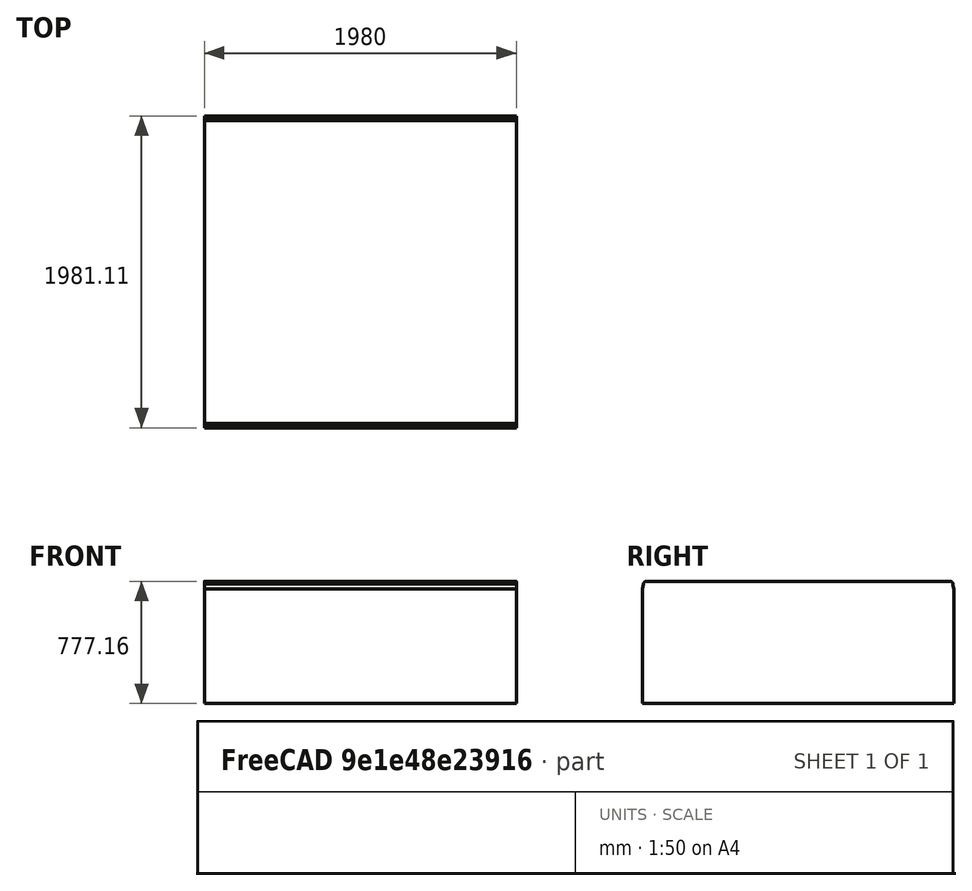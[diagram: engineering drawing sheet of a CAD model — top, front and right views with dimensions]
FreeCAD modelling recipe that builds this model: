
FCSTD DOCUMENT  (FreeCAD 0.20R29177 (Git))
Label: banheira2
License: All rights reserved
LicenseURL: http://en.wikipedia.org/wiki/All_rights_reserved
objects: Sketcher::SketchObject×2, Image::ImagePlane×1, PartDesign::Pad×1, PartDesign::Body×1
note: 5 computed .brp shape members not serialized (recipe doc carries the construction recipe); baked Part::Feature solids carry a one-line shape summary decoded from their .brp

FEATURE [Image::ImagePlane] ImagePlane
  Placement = pos=(0,0,0) rot=(0.57735,0.57735,0.57735;2.0944rad)
  XSize = 2368.8
  YSize = 1776.6
FEATURE [Sketcher::SketchObject] Sketch
  FullyConstrained = false
  MapMode = 5
  Placement = pos=(0,0,0) rot=(0.57735,0.57735,0.57735;2.0944rad)
  Support = -> [YZ_Plane]
  sketch-geometry (16):
    g0: LineSegment StartX=1058.18 StartY=310.927 StartZ=0 EndX=1051.75 EndY=340.953 EndZ=0
    g1: LineSegment StartX=-922.934 StartY=315.236 StartZ=0 EndX=-915.586 EndY=347.382 EndZ=0
    g2: ArcOfCircle CenterX=-895.394 CenterY=342.098 CenterZ=0 NormalX=0 NormalY=0 NormalZ=1 AngleXU=0 Radius=20.8727 StartAngle=1.52646 EndAngle=2.88566
    g3: ArcOfCircle CenterX=1031.59 CenterY=342.885 CenterZ=0 NormalX=0 NormalY=0 NormalZ=1 AngleXU=0 Radius=20.259 StartAngle=6.18766 EndAngle=7.99238
    g4: LineSegment StartX=1028.79 StartY=362.951 StartZ=0 EndX=-894.468 EndY=362.951 EndZ=0
    g5: LineSegment StartX=-922.934 StartY=315.236 StartZ=0 EndX=-922.934 EndY=-414.021 EndZ=0
    g6: LineSegment StartX=166.359 StartY=-414.021 StartZ=0 EndX=1058.18 EndY=-414.021 EndZ=0
    g7: LineSegment StartX=166.359 StartY=-414.021 StartZ=0 EndX=-922.934 EndY=-414.021 EndZ=0
    g8: LineSegment StartX=1058.18 StartY=310.927 StartZ=0 EndX=1058.18 EndY=-414.021 EndZ=0
    g9: GeomPoint X=-922.934 Y=315.236 Z=0
    g10: GeomPoint X=-915.586 Y=347.382 Z=0
    g11: GeomPoint X=-894.468 Y=362.951 Z=0
    g12: GeomPoint X=1028.79 Y=362.951 Z=0
    g13: GeomPoint X=1051.75 Y=340.953 Z=0
    g14: GeomPoint X=1058.18 Y=310.927 Z=0
    g15: GeomPoint X=1058.18 Y=-414.021 Z=0
  constraints (19):
    c: Coincident(g5,g7)
    c: Vertical(g5)
    c: Horizontal(g7)
    c: Coincident(g7,g6)
    c: Coincident(g8,g6)
    c: Coincident(g8,g0)
    c: Coincident(g3,g0)
    c: Coincident(g3,g4)
    c: Coincident(g2,g4)
    c: Coincident(g2,g1)
    c: Coincident(g5,g1)
    c: Block(g5)
    c: Block(g1)
    c: Block(g2)
    c: Block(g4)
    c: Block(g3)
    c: Block(g0)
    c: Block(g8)
    c: Block(g6)
FEATURE [PartDesign::Pad] Pad
  Direction = (1,-2e-16,3e-16)
  Length = 1980
  Length2 = 10
  Placement = pos=(0,0,0) rot=(0.57735,0.57735,0.57735;2.0944rad)
  Profile = -> Sketch
  ReferenceAxis = -> Sketch [N_Axis]
  Reversed = true
  Type = 0
FEATURE [Sketcher::SketchObject] Sketch001
  ExternalGeometry = -> [Pad]
  FullyConstrained = true
  MapMode = 5
  Placement = pos=(-1980,8.793e-13,-6.595e-13) rot=(0.57735,0.57735,-0.57735;4.18879rad)
  Support = -> [Pad]
  sketch-geometry (4):
    g0: LineSegment StartX=-922.934 StartY=-315.236 StartZ=0 EndX=1058.18 EndY=-315.236 EndZ=0
    g1: LineSegment StartX=1058.18 StartY=-315.236 StartZ=0 EndX=1058.18 EndY=414.021 EndZ=0
    g2: LineSegment StartX=1058.18 StartY=414.021 StartZ=0 EndX=-922.934 EndY=414.021 EndZ=0
    g3: LineSegment StartX=-922.934 StartY=414.021 StartZ=0 EndX=-922.934 EndY=-315.236 EndZ=0
  constraints (10):
    c: Coincident(g0,g1)
    c: Coincident(g1,g2)
    c: Coincident(g2,g3)
    c: Coincident(g3,g0)
    c: Horizontal(g0)
    c: Horizontal(g2)
    c: Vertical(g1)
    c: Vertical(g3)
    c: Coincident(g0,g-3)
    c: Coincident(g1,g-5)
FEATURE [PartDesign::Body] Body
  Group = -> [Sketch,Pad,Sketch001]
  Origin = -> Origin
  Tip = -> Pad
